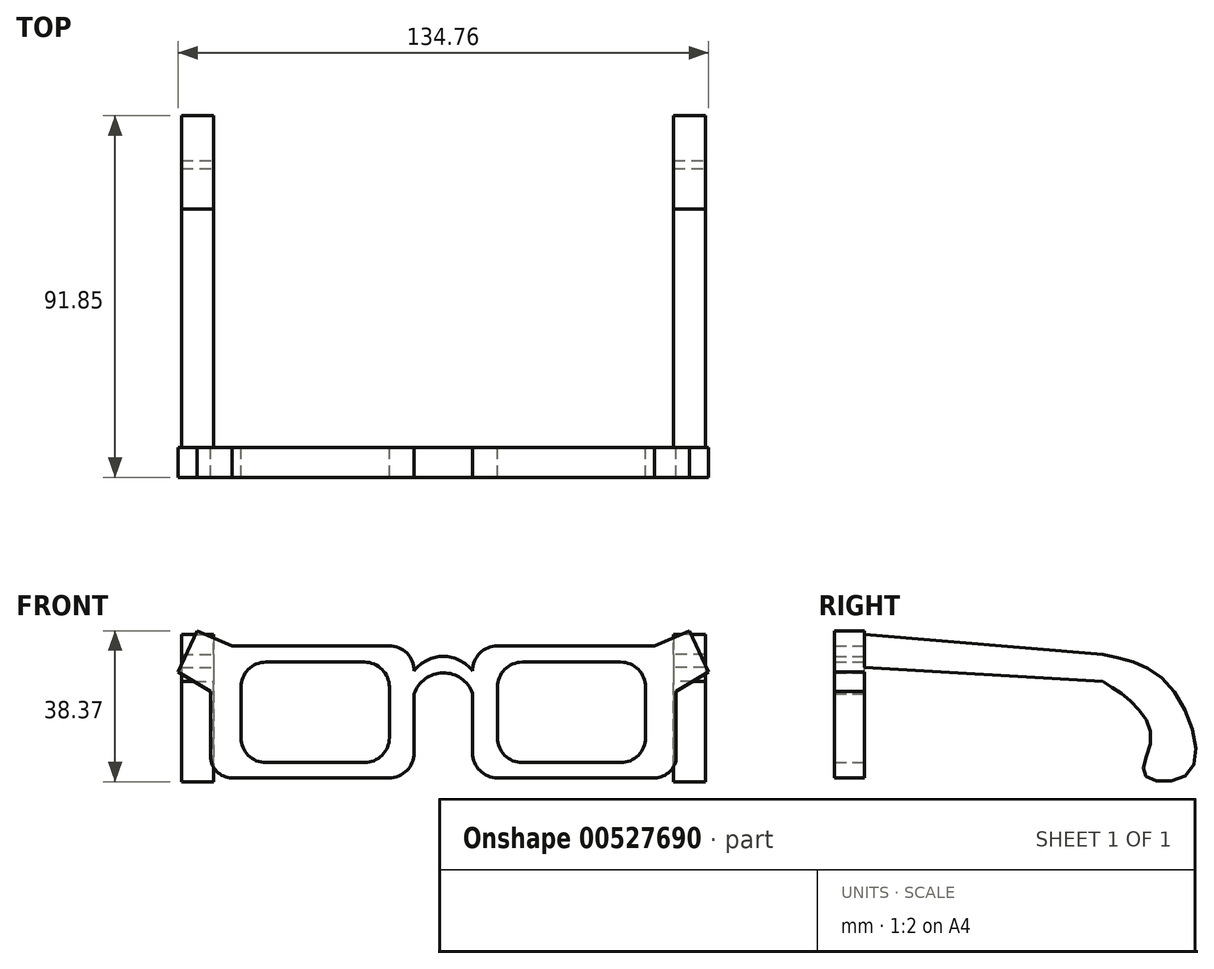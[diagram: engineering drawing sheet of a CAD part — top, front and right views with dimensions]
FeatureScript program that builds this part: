
annotation { "Feature Type Name" : "Feature", "Feature Type Description" : "" }
export const myFeature = defineFeature(function(context is Context, id is Id, definition is map)
    precondition{}
    {
        {
            var Q0;
            Q0=qCreatedBy(makeId("Front.planeOp"),FACE);
            var sketch = newSketch(context, id + "F0", { "sketchPlane" : qUnion([Q0])});
            skLineSegment(sketch, "E0.bottom", {"start": v(20.07, 14.81) * mm, "end": v(45.06, 14.81) * mm});
            skLineSegment(sketch, "E0.top", {"start": v(20.07, -10.72) * mm, "end": v(45.06, -10.72) * mm});
            skLineSegment(sketch, "E0.left", {"start": v(13.72, 8.46) * mm, "end": v(13.72, -4.37) * mm});
            skLineSegment(sketch, "E0.right", {"start": v(51.4, 8.46) * mm, "end": v(51.4, -4.37) * mm});
            skPoint(sketch, "E1.visualSharp", {"position": v(13.72, 14.81) * mm});
            skArc(sketch, "E1.filletArc", {"start": v(20.07, 14.81) * mm, "mid": v(15.58, 12.95) * mm, "end": v(13.72, 8.46) * mm});
            skPoint(sketch, "E2.visualSharp", {"position": v(13.72, -10.72) * mm});
            skArc(sketch, "E2.filletArc", {"start": v(13.72, -4.37) * mm, "mid": v(15.58, -8.86) * mm, "end": v(20.07, -10.72) * mm});
            skPoint(sketch, "E3.visualSharp", {"position": v(51.4, -10.72) * mm});
            skArc(sketch, "E3.filletArc", {"start": v(45.06, -10.72) * mm, "mid": v(49.55, -8.86) * mm, "end": v(51.4, -4.37) * mm});
            skPoint(sketch, "E4.visualSharp", {"position": v(51.4, 14.81) * mm});
            skArc(sketch, "E4.filletArc", {"start": v(51.4, 8.46) * mm, "mid": v(49.55, 12.95) * mm, "end": v(45.06, 14.81) * mm});
            skLineSegment(sketch, "E5.MirrorCS", {"start": v(-20.07, 14.81) * mm, "end": v(-45.06, 14.81) * mm});
            skPoint(sketch, "E6.MirrorP", {"position": v(-13.72, 14.81) * mm});
            skArc(sketch, "E7.MirrorCS", {"start": v(-20.07, 14.81) * mm, "mid": v(-15.58, 12.95) * mm, "end": v(-13.72, 8.46) * mm});
            skLineSegment(sketch, "E8.MirrorCS", {"start": v(-13.72, 8.46) * mm, "end": v(-13.72, -4.37) * mm});
            skArc(sketch, "E9.MirrorCS", {"start": v(-13.72, -4.37) * mm, "mid": v(-15.58, -8.86) * mm, "end": v(-20.07, -10.72) * mm});
            skLineSegment(sketch, "E10.MirrorCS", {"start": v(-20.07, -10.72) * mm, "end": v(-45.06, -10.72) * mm});
            skArc(sketch, "E11.MirrorCS", {"start": v(-45.06, -10.72) * mm, "mid": v(-49.55, -8.86) * mm, "end": v(-51.4, -4.37) * mm});
            skLineSegment(sketch, "E12.MirrorCS", {"start": v(-51.4, 8.46) * mm, "end": v(-51.4, -4.37) * mm});
            skArc(sketch, "E13.MirrorCS", {"start": v(-51.4, 8.46) * mm, "mid": v(-49.55, 12.95) * mm, "end": v(-45.06, 14.81) * mm});
            skSolve(sketch);
        }
        {
            var Q0;
            Q0=qCreatedBy(makeId("Front.planeOp"),FACE);
            var sketch = newSketch(context, id + "F1", { "sketchPlane" : qUnion([Q0])});
            skLineSegment(sketch, "E14.bottom", {"start": v(13.77, 18.96) * mm, "end": v(53.68, 18.96) * mm});
            skLineSegment(sketch, "E14.top", {"start": v(13.77, -14.58) * mm, "end": v(53.68, -14.58) * mm});
            skLineSegment(sketch, "E14.left", {"start": v(7.42, 6.9) * mm, "end": v(7.42, -8.23) * mm});
            skLineSegment(sketch, "E14.right", {"start": v(59.16, 7.41) * mm, "end": v(59.16, -9.1) * mm});
            skPoint(sketch, "E15.visualSharp", {"position": v(59.16, 18.96) * mm});
            skPoint(sketch, "E16.visualSharp", {"position": v(7.42, 18.96) * mm});
            skArc(sketch, "E16.filletArc", {"start": v(13.77, 18.96) * mm, "mid": v(9.28, 17.1) * mm, "end": v(7.42, 12.6) * mm});
            skPoint(sketch, "E17.visualSharp", {"position": v(7.42, -14.58) * mm});
            skArc(sketch, "E17.filletArc", {"start": v(7.42, -8.23) * mm, "mid": v(9.28, -12.72) * mm, "end": v(13.77, -14.58) * mm});
            skPoint(sketch, "E18.visualSharp", {"position": v(59.16, -14.58) * mm});
            skArc(sketch, "E18.filletArc", {"start": v(53.68, -14.58) * mm, "mid": v(57.56, -12.97) * mm, "end": v(59.16, -9.1) * mm});
            skLineSegment(sketch, "E19", {"start": v(53.68, 18.96) * mm, "end": v(62.56, 22.79) * mm});
            skLineSegment(sketch, "E20", {"start": v(59.16, 7.41) * mm, "end": v(67.38, 12.34) * mm});
            skLineSegment(sketch, "E21", {"start": v(62.56, 22.79) * mm, "end": v(67.38, 12.34) * mm});
            skLineSegment(sketch, "E22.MirrorCS", {"start": v(-13.77, 18.96) * mm, "end": v(-53.68, 18.96) * mm});
            skArc(sketch, "E23.MirrorCS", {"start": v(-13.77, 18.96) * mm, "mid": v(-9.28, 17.1) * mm, "end": v(-7.42, 12.6) * mm});
            skLineSegment(sketch, "E24.MirrorCS", {"start": v(-7.42, 6.7) * mm, "end": v(-7.42, -8.23) * mm});
            skArc(sketch, "E25.MirrorCS", {"start": v(-7.42, -8.23) * mm, "mid": v(-9.28, -12.72) * mm, "end": v(-13.77, -14.58) * mm});
            skLineSegment(sketch, "E26.MirrorCS", {"start": v(-13.77, -14.58) * mm, "end": v(-53.68, -14.58) * mm});
            skLineSegment(sketch, "E27.MirrorCS", {"start": v(-59.16, 7.41) * mm, "end": v(-59.16, -9.1) * mm});
            skLineSegment(sketch, "E28.MirrorCS", {"start": v(-59.16, 7.41) * mm, "end": v(-67.38, 12.34) * mm});
            skLineSegment(sketch, "E29.MirrorCS", {"start": v(-62.56, 22.79) * mm, "end": v(-67.38, 12.34) * mm});
            skLineSegment(sketch, "E30.MirrorCS", {"start": v(-53.68, 18.96) * mm, "end": v(-62.56, 22.79) * mm});
            skArc(sketch, "E31.MirrorCS", {"start": v(-53.68, -14.58) * mm, "mid": v(-57.56, -12.97) * mm, "end": v(-59.16, -9.1) * mm});
            skArc(sketch, "E32", {"start": v(7.42, 12.6) * mm, "mid": v(0, 16.27) * mm, "end": v(-7.42, 12.6) * mm});
            skArc(sketch, "E33", {"start": v(7.42, 6.9) * mm, "mid": v(-0.07, 12.07) * mm, "end": v(-7.42, 6.7) * mm});
            skPoint(sketch, "E34.orphan", {"position": v(-7.42, 12.6) * mm});
            skSolve(sketch);
        }
        {
            var Q0;
            Q0=makeQuery(id+"F0.imprint","IMPRINT",FACE,{"disambiguationData":[TD([[makeQuery(id+"F0.imprint","IMPRINT",EDGE,{"derivedFrom":sQuery(id+"F0.wireOp",EDGE,"E0.bottom")}),-1.0]])]});
            var Q1;
            Q1=makeQuery(id+"F0.imprint","IMPRINT",FACE,{"disambiguationData":[TD([[makeQuery(id+"F0.imprint","IMPRINT",EDGE,{"derivedFrom":sQuery(id+"F0.wireOp",EDGE,"E5.MirrorCS")}),1.0]])]});
            var Q2;
            Q2=makeQuery(id+"F1.imprint","IMPRINT",FACE,{"disambiguationData":[TD([[makeQuery(id+"F1.imprint","IMPRINT",EDGE,{"derivedFrom":sQuery(id+"F1.wireOp",EDGE,"E14.bottom")}),-1.0]])]});
            extrude(context, id + "F2", {"entities" : qUnion([Q0, Q1, Q2]), "depth" : 7.62 * mm, "offsetDistance" : 25.4 * mm});
        }
        {
            var Q0;
            Q0=qCreatedBy(makeId("Right.planeOp"),FACE);
            var sketch = newSketch(context, id + "F3", { "sketchPlane" : qUnion([Q0])});
            skLineSegment(sketch, "E35", {"start": v(0, 21.81) * mm, "end": v(0, 13.47) * mm});
            skLineSegment(sketch, "E36", {"start": v(0, 13.47) * mm, "end": v(60.56, 9.9) * mm});
            skLineSegment(sketch, "E37", {"start": v(60.56, 16.74) * mm, "end": v(0, 21.81) * mm});
            skFitSpline(sketch, "E38", {"points": [v(60.56, 16.74) * mm, v(77.24, 9) * mm, v(82.6, -13.05) * mm, v(71.28, -13.95) * mm, v(72.77, -4.71) * mm, v(68, 4.53) * mm, v(60.56, 9.9) * mm], "startDerivative": vector(90.16, -17.41) * mm, "endDerivative": vector(-54.12, 33.36) * mm});
            skSolve(sketch);
        }
        {
            var Q0;
            Q0=makeQuery(id+"F3.imprint","IMPRINT",FACE,{"disambiguationData":[TD([[makeQuery(id+"F3.imprint","IMPRINT",EDGE,{"derivedFrom":sQuery(id+"F3.wireOp",EDGE,"E35")}),1.0]])]});
            extrude(context, id + "F4", {"entities" : qUnion([Q0]), "depth" : 8.13 * mm, "offsetDistance" : 25.4 * mm});
        }
        {
            var Q0;
            Q0=makeQuery(id+"F4.opExtrude","SWEPT_BODY",BODY,{"disambiguationData":[OSD([sQuery(id+"F3.wireOp",EDGE,"E35"),sQuery(id+"F3.wireOp",EDGE,"E36"),sQuery(id+"F3.wireOp",EDGE,"E37"),sQuery(id+"F3.wireOp",EDGE,"E38")])]});
            transform(context, id + "F5", {"entities" : qUnion([Q0]), "transformType" : TransformType.TRANSLATION_3D, "dx" : 58.42 * mm, "dy" : 0 * mm, "dz" : 0 * mm, "makeCopy" : false});
        }
        {
            var Q0;
            Q0=makeQuery(id+"F4.opExtrude","SWEPT_BODY",BODY,{"disambiguationData":[OSD([sQuery(id+"F3.wireOp",EDGE,"E35"),sQuery(id+"F3.wireOp",EDGE,"E36"),sQuery(id+"F3.wireOp",EDGE,"E37"),sQuery(id+"F3.wireOp",EDGE,"E38")])]});
            var Q1;
            Q1=qCreatedBy(makeId("Right.planeOp"),FACE);
            mirror(context, id + "F6", {"entities" : qUnion([Q0]), "mirrorPlane" : qUnion([Q1])});
        }
    });
